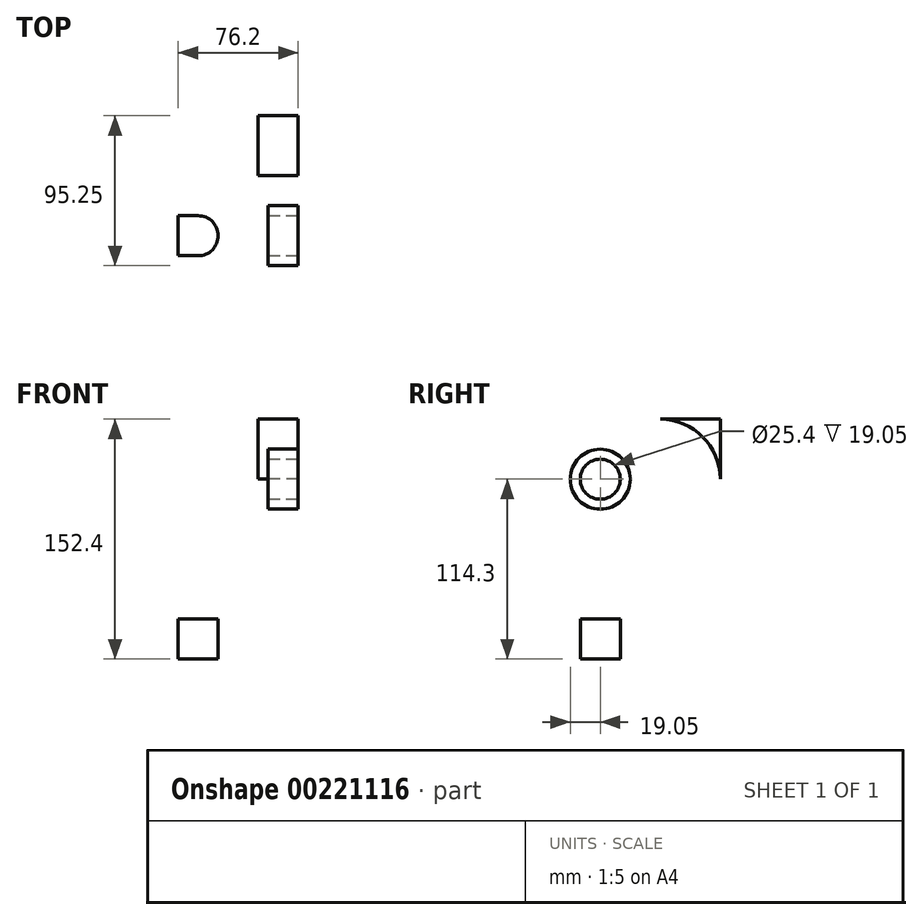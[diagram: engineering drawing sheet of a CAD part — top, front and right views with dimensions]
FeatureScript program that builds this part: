
annotation { "Feature Type Name" : "Feature", "Feature Type Description" : "" }
export const myFeature = defineFeature(function(context is Context, id is Id, definition is map)
    precondition{}
    {
        {
            var Q0;
            Q0=qCreatedBy(makeId("Front.planeOp"),FACE);
            var sketch = newSketch(context, id + "F0", { "sketchPlane" : qUnion([Q0])});
            skLineSegment(sketch, "E0", {"start": v(0, 0) * mm, "end": v(0, 152.4) * mm});
            skLineSegment(sketch, "E1", {"start": v(0, 152.4) * mm, "end": v(-25.4, 152.4) * mm});
            skLineSegment(sketch, "E2", {"start": v(-25.4, 152.4) * mm, "end": v(-25.4, 25.4) * mm});
            skLineSegment(sketch, "E3", {"start": v(-25.4, 25.4) * mm, "end": v(-76.2, 25.4) * mm});
            skLineSegment(sketch, "E4", {"start": v(-76.2, 25.4) * mm, "end": v(-76.2, 0) * mm});
            skLineSegment(sketch, "E5", {"start": v(-76.2, 0) * mm, "end": v(0, 0) * mm});
            skSolve(sketch);
        }
        {
            var Q0;
            Q0 = qSketchRegion(id + "F0", true);
            extrude(context, id + "F1", {"entities" : qUnion([Q0]), "endBound" : BoundingType.SYMMETRIC, "depth" : 152.4 * mm});
        }
        {
            var Q0;
            Q0=makeQuery(id+"F1.opExtrude","SWEPT_FACE",FACE,{"disambiguationData":[OSD([sQuery(id+"F0.wireOp",EDGE,"E0")])]});
            var sketch = newSketch(context, id + "F2", { "sketchPlane" : qUnion([Q0])});
            skCircle(sketch, "E6", {"center": v(0, 114.3) * mm, "radius": 12.7 * mm});
            skPoint(sketch, "E6.centerSnap0", {"position": v(0, 152.4) * mm});
            skSolve(sketch);
        }
        {
            var Q0;
            Q0=makeQuery(id+"F2.imprint","IMPRINT",FACE,{"disambiguationData":[TD([[makeQuery(id+"F2.imprint","IMPRINT",EDGE,{"derivedFrom":sQuery(id+"F2.wireOp",EDGE,"E6")}),1.0]])]});
            extrude(context, id + "F3", {"entities" : qUnion([Q0]), "operationType" : NewBodyOperationType.REMOVE, "endBound" : BoundingType.THROUGH_ALL, "oppositeDirection" : true, "depth" : 25.4 * mm});
        }
        {
            var Q0;
            Q0=makeQuery(id+"F1.opExtrude","SWEPT_FACE",FACE,{"disambiguationData":[OSD([sQuery(id+"F0.wireOp",EDGE,"E3")])]});
            var sketch = newSketch(context, id + "F4", { "sketchPlane" : qUnion([Q0])});
            skPoint(sketch, "E7.centerSnap0", {"position": v(-76.2, 0) * mm});
            skArc(sketch, "E8", {"start": v(-63.5, 12.7) * mm, "mid": v(-50.8, 0) * mm, "end": v(-63.5, -12.7) * mm});
            skLineSegment(sketch, "E9", {"start": v(-76.2, 12.7) * mm, "end": v(-63.5, 12.7) * mm});
            skLineSegment(sketch, "E10", {"start": v(-76.2, -12.7) * mm, "end": v(-63.5, -12.7) * mm});
            skSolve(sketch);
        }
        {
            var Q0;
            Q0=makeQuery(id+"F4.imprint","IMPRINT",FACE,{"disambiguationData":[TD([[makeQuery(id+"F4.imprint","IMPRINT",EDGE,{"derivedFrom":sQuery(id+"F4.wireOp",EDGE,"E8")}),-1.0]])]});
            extrude(context, id + "F5", {"entities" : qUnion([Q0]), "operationType" : NewBodyOperationType.REMOVE, "endBound" : BoundingType.THROUGH_ALL, "oppositeDirection" : true, "depth" : 25.4 * mm});
        }
        {
            var Q0;
            Q0=makeQuery(id+"F1.opExtrude","SWEPT_FACE",FACE,{"disambiguationData":[OSD([sQuery(id+"F0.wireOp",EDGE,"E2")])]});
            var sketch = newSketch(context, id + "F6", { "sketchPlane" : qUnion([Q0])});
            skCircle(sketch, "E11", {"center": v(0, 114.3) * mm, "radius": 19.05 * mm});
            skSolve(sketch);
        }
        {
            var Q0;
            Q0=makeQuery(id+"F6.imprint","IMPRINT",FACE,{"disambiguationData":[TD([[makeQuery(id+"F6.imprint","IMPRINT",EDGE,{"derivedFrom":sQuery(id+"F6.wireOp",EDGE,"E11")}),1.0]])]});
            extrude(context, id + "F7", {"entities" : qUnion([Q0]), "operationType" : NewBodyOperationType.REMOVE, "oppositeDirection" : true, "depth" : 6.35 * mm});
        }
        {
            var Q0;
            Q0=makeQuery(id+"F1.opExtrude","SWEPT_FACE",FACE,{"disambiguationData":[OSD([sQuery(id+"F0.wireOp",EDGE,"E2")])]});
            var sketch = newSketch(context, id + "F8", { "sketchPlane" : qUnion([Q0])});
            skArc(sketch, "E12", {"start": v(76.2, 114.3) * mm, "mid": v(65.04, 141.24) * mm, "end": v(38.1, 152.4) * mm});
            skArc(sketch, "E13.MirrorCS", {"start": v(-76.2, 114.3) * mm, "mid": v(-65.04, 141.24) * mm, "end": v(-38.1, 152.4) * mm});
            skSolve(sketch);
        }
        {
            var Q0;
            {var subQ0=sQuery(id+"F8.wireOp",EDGE,"E13.MirrorCS");Q0=makeQuery(id+"F8.imprint","IMPRINT",FACE,{"disambiguationData":[TD([[makeQuery(id+"F8.imprint","IMPRINT",EDGE,{"derivedFrom":subQ0}),1.0]])]});}
            var Q1;
            {var subQ0=sQuery(id+"F8.wireOp",EDGE,"E12");Q1=makeQuery(id+"F8.imprint","IMPRINT",FACE,{"disambiguationData":[TD([[makeQuery(id+"F8.imprint","IMPRINT",EDGE,{"derivedFrom":subQ0}),-1.0]])]});}
            extrude(context, id + "F9", {"entities" : qUnion([Q0, Q1]), "operationType" : NewBodyOperationType.REMOVE, "endBound" : BoundingType.THROUGH_ALL, "oppositeDirection" : true, "depth" : 25.4 * mm});
        }
    });
